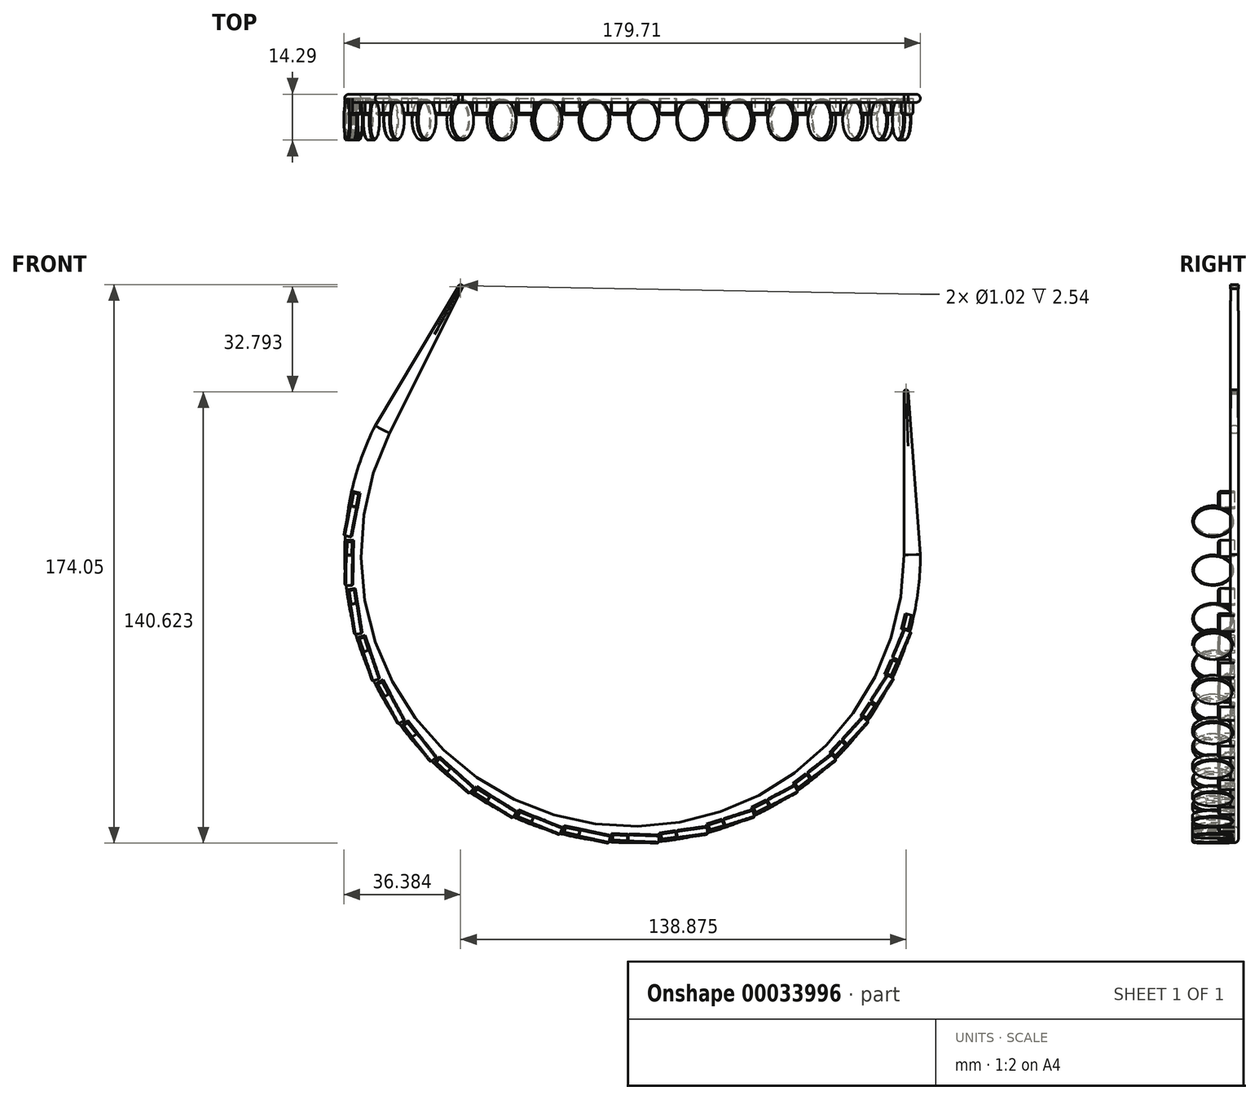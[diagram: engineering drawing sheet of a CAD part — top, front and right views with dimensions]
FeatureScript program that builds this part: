
annotation { "Feature Type Name" : "Feature", "Feature Type Description" : "" }
export const myFeature = defineFeature(function(context is Context, id is Id, definition is map)
    precondition{}
    {
        {
            var Q0;
            Q0=qCreatedBy(makeId("Front.planeOp"),FACE);
            var sketch = newSketch(context, id + "F0", { "sketchPlane" : qUnion([Q0])});
            skArc(sketch, "E0", {"start": v(-188.33, 16.19) * mm, "mid": v(-128.74, -111.39) * mm, "end": v(-18.36, -23.95) * mm});
            skArc(sketch, "E1", {"start": v(-23.44, -24.04) * mm, "mid": v(-127.57, -106.44) * mm, "end": v(-183.83, 13.83) * mm});
            skLineSegment(sketch, "E2", {"start": v(-183.83, 13.83) * mm, "end": v(-161.1, 59.27) * mm});
            skLineSegment(sketch, "E3", {"start": v(-188.33, 16.19) * mm, "end": v(-162.27, 59.79) * mm});
            skLineSegment(sketch, "E4", {"start": v(-162.27, 59.79) * mm, "end": v(-161.1, 59.27) * mm});
            skLineSegment(sketch, "E5", {"start": v(-18.36, -23.95) * mm, "end": v(-22.17, 26.7) * mm});
            skLineSegment(sketch, "E6", {"start": v(-23.44, -24.04) * mm, "end": v(-23.44, 26.76) * mm});
            skLineSegment(sketch, "E7", {"start": v(-23.44, 26.76) * mm, "end": v(-22.17, 26.7) * mm});
            skLineSegment(sketch, "E8", {"start": v(-188.33, 16.19) * mm, "end": v(-183.83, 13.83) * mm});
            skLineSegment(sketch, "E9", {"start": v(-23.44, -24.04) * mm, "end": v(-18.36, -23.95) * mm});
            skSolve(sketch);
        }
        {
            var Q0;
            Q0=makeQuery(id+"F0.imprint","IMPRINT",FACE,{"disambiguationData":[TD([[makeQuery(id+"F0.imprint","IMPRINT",EDGE,{"derivedFrom":sQuery(id+"F0.wireOp",EDGE,"E0")}),1.0]])]});
            var sketch = newSketch(context, id + "F1", { "sketchPlane" : qUnion([Q0])});
            skSolve(sketch);
        }
        {
            var Q0;
            Q0=makeQuery(id+"F1.imprint","IMPRINT",FACE,{"disambiguationData":[TD([[makeQuery(id+"F1.imprint","IMPRINT",EDGE,{"derivedFrom":makeQuery(id+"F0.imprint","IMPRINT",EDGE,{"derivedFrom":sQuery(id+"F0.wireOp",EDGE,"E0")})}),1.0]])]});
            extrude(context, id + "F2", {"entities" : qUnion([Q0]), "depth" : 2.54 * mm});
        }
        {
            var Q0;
            Q0=makeQuery(id+"F0.imprint","IMPRINT",FACE,{"disambiguationData":[TD([[makeQuery(id+"F0.imprint","IMPRINT",EDGE,{"derivedFrom":sQuery(id+"F0.wireOp",EDGE,"E2")}),1.0]])]});
            var sketch = newSketch(context, id + "F3", { "sketchPlane" : qUnion([Q0])});
            skCircle(sketch, "E10", {"center": v(-161.69, 59.53) * mm, "radius": 0.63 * mm});
            skPoint(sketch, "E10.first.point", {"position": v(-162.3, 59.7) * mm});
            skPoint(sketch, "E10.second.point", {"position": v(-161.15, 59.2) * mm});
            skPoint(sketch, "E10.third.point", {"position": v(-161.2, 59.93) * mm});
            skCircle(sketch, "E11", {"center": v(-161.69, 59.53) * mm, "radius": 0.5 * mm});
            skSolve(sketch);
        }
        {
            var Q0;
            Q0 = qSketchRegion(id + "F3", true);
            extrude(context, id + "F4", {"entities" : qUnion([Q0]), "depth" : 2.54 * mm});
        }
        {
            var Q0;
            Q0=makeQuery(id+"F0.imprint","IMPRINT",FACE,{"disambiguationData":[TD([[makeQuery(id+"F0.imprint","IMPRINT",EDGE,{"derivedFrom":sQuery(id+"F0.wireOp",EDGE,"E5")}),1.0]])]});
            var sketch = newSketch(context, id + "F5", { "sketchPlane" : qUnion([Q0])});
            skCircle(sketch, "E12", {"center": v(-22.81, 26.73) * mm, "radius": 0.63 * mm});
            skPoint(sketch, "E12.first.point", {"position": v(-23.44, 26.78) * mm});
            skPoint(sketch, "E12.second.point", {"position": v(-22.18, 26.72) * mm});
            skPoint(sketch, "E12.third.point", {"position": v(-22.6, 27.33) * mm});
            skCircle(sketch, "E13", {"center": v(-22.81, 26.73) * mm, "radius": 0.5 * mm});
            skSolve(sketch);
        }
        {
            var Q0;
            Q0 = qSketchRegion(id + "F5", true);
            extrude(context, id + "F6", {"entities" : qUnion([Q0]), "depth" : 2.54 * mm});
        }
        {
            var Q0;
            Q0=makeQuery(id+"F0.imprint","IMPRINT",FACE,{"disambiguationData":[TD([[makeQuery(id+"F0.imprint","IMPRINT",EDGE,{"derivedFrom":sQuery(id+"F0.wireOp",EDGE,"E5")}),1.0]])]});
            var Q1;
            Q1=makeQuery(id+"F0.imprint","IMPRINT",FACE,{"disambiguationData":[TD([[makeQuery(id+"F0.imprint","IMPRINT",EDGE,{"derivedFrom":sQuery(id+"F0.wireOp",EDGE,"E2")}),1.0]])]});
            extrude(context, id + "F7", {"entities" : qUnion([Q0, Q1]), "depth" : 2.54 * mm});
        }
        {
            var Q0;
            Q0=makeQuery(id+"F7.opExtrude","SWEPT_FACE",FACE,{"disambiguationData":[OSD([sQuery(id+"F0.wireOp",EDGE,"E3")])]});
            var sketch = newSketch(context, id + "F8", { "sketchPlane" : qUnion([Q0])});
            skEllipse(sketch, "E14", {"center": v(7.94, -82.75) * mm, "majorRadius": 6.35 * mm, "minorRadius": 4.76 * mm, "majorAxis": v(1, 0)});
            skSolve(sketch);
        }
        {
            var Q0;
            {var subQ0=sQuery(id+"F8.wireOp",EDGE,"E14");var subQ1=sQuery(id+"F0.wireOp",EDGE,"E3");var subQ4=makeQuery(id+"F7.opExtrude","CAP_EDGE",EDGE,{"disambiguationData":[OSD([subQ1])],"isStart":false});var subQ5=makeQuery(id+"F8.imprint","INTERSECT",VERTEX,{"derivedFrom":[subQ4,subQ0]});Q0=makeQuery(id+"F8.imprint","IMPRINT",FACE,{"disambiguationData":[TD([[makeQuery(id+"F8.imprint","IMPRINT",EDGE,{"disambiguationData":[TD([[subQ5,1.0]])],"derivedFrom":subQ0}),1.0]])]});}
            var Q1;
            {var subQ0=sQuery(id+"F8.wireOp",EDGE,"E14");var subQ1=sQuery(id+"F0.wireOp",EDGE,"E3");var subQ4=makeQuery(id+"F7.opExtrude","CAP_EDGE",EDGE,{"disambiguationData":[OSD([subQ1])],"isStart":false});var subQ5=makeQuery(id+"F8.imprint","INTERSECT",VERTEX,{"derivedFrom":[subQ4,subQ0]});Q1=makeQuery(id+"F8.imprint","IMPRINT",FACE,{"disambiguationData":[TD([[makeQuery(id+"F8.imprint","IMPRINT",EDGE,{"disambiguationData":[TD([[subQ5,-1.0]])],"derivedFrom":subQ0}),1.0]])]});}
            extrude(context, id + "F9", {"entities" : qUnion([Q0, Q1]), "oppositeDirection" : true, "depth" : 2.54 * mm});
        }
        {
            var Q0;
            Q0=makeQuery(id+"F9.opExtrude","CAP_EDGE",EDGE,{"disambiguationData":[OSD([sQuery(id+"F8.wireOp",EDGE,"E14")])],"isStart":true});
            var Q1;
            Q1=makeQuery(id+"F9.opExtrude","CAP_EDGE",EDGE,{"disambiguationData":[OSD([sQuery(id+"F8.wireOp",EDGE,"E14")])],"isStart":false});
            chamfer(context, id + "F10", {"entities" : qUnion([Q0, Q1]), "width" : 0.32 * mm, "tangentPropagation" : true});
        }
        {
            var Q0;
            Q0=makeQuery(id+"F2.opExtrude","CAP_EDGE",EDGE,{"disambiguationData":[OSD([sQuery(id+"F0.wireOp",EDGE,"E0")])],"isStart":true});
            var Q1;
            Q1=makeQuery(id+"F2.opExtrude","CAP_EDGE",EDGE,{"disambiguationData":[OSD([sQuery(id+"F0.wireOp",EDGE,"E0")])],"isStart":false});
            var Q2;
            Q2=makeQuery(id+"F2.opExtrude","CAP_EDGE",EDGE,{"disambiguationData":[OSD([sQuery(id+"F0.wireOp",EDGE,"E1")])],"isStart":false});
            var Q3;
            Q3=makeQuery(id+"F2.opExtrude","CAP_EDGE",EDGE,{"disambiguationData":[OSD([sQuery(id+"F0.wireOp",EDGE,"E1")])],"isStart":true});
            fillet(context, id + "F11", {"entities" : qUnion([Q0, Q1, Q2, Q3]), "radius" : 1.27 * mm, "tangentPropagation" : true, "allowEdgeOverflow" : false});
        }
        {
            var Q0;
            Q0=makeQuery(id+"F7.opExtrude","CAP_EDGE",EDGE,{"disambiguationData":[OSD([sQuery(id+"F0.wireOp",EDGE,"E6")])],"isStart":true});
            var Q1;
            Q1=makeQuery(id+"F7.opExtrude","CAP_EDGE",EDGE,{"disambiguationData":[OSD([sQuery(id+"F0.wireOp",EDGE,"E6")])],"isStart":false});
            var Q2;
            Q2=makeQuery(id+"F7.opExtrude","CAP_EDGE",EDGE,{"disambiguationData":[OSD([sQuery(id+"F0.wireOp",EDGE,"E5")])],"isStart":false});
            var Q3;
            Q3=makeQuery(id+"F7.opExtrude","CAP_EDGE",EDGE,{"disambiguationData":[OSD([sQuery(id+"F0.wireOp",EDGE,"E3")])],"isStart":true});
            var Q4;
            Q4=makeQuery(id+"F7.opExtrude","CAP_EDGE",EDGE,{"disambiguationData":[OSD([sQuery(id+"F0.wireOp",EDGE,"E3")])],"isStart":false});
            var Q5;
            Q5=makeQuery(id+"F7.opExtrude","CAP_EDGE",EDGE,{"disambiguationData":[OSD([sQuery(id+"F0.wireOp",EDGE,"E2")])],"isStart":false});
            var Q6;
            Q6=makeQuery(id+"F7.opExtrude","CAP_EDGE",EDGE,{"disambiguationData":[OSD([sQuery(id+"F0.wireOp",EDGE,"E2")])],"isStart":true});
            var Q7;
            Q7=makeQuery(id+"F7.opExtrude","CAP_EDGE",EDGE,{"disambiguationData":[OSD([sQuery(id+"F0.wireOp",EDGE,"E5")])],"isStart":true});
            fillet(context, id + "F12", {"entities" : qUnion([Q0, Q1, Q2, Q3, Q4, Q5, Q6, Q7]), "radius" : 1.27 * mm, "tangentPropagation" : true, "allowEdgeOverflow" : false});
        }
        {
            var Q0;
            Q0=makeQuery(id+"F9.opExtrude","SWEPT_BODY",BODY,{"disambiguationData":[OSD([sQuery(id+"F8.wireOp",EDGE,"E14")])]});
            var Q1;
            Q1=makeQuery(id+"F11.opFillet","BLEND_FACE",FACE,{"disambiguationData":[OSD([sQuery(id+"F0.wireOp",EDGE,"E0")])]});
            circularPattern(context, id + "F13", {"entities" : qUnion([Q0]), "axis" : qUnion([Q1]), "angle" : 9.9 * degree, "instanceCount" : 22});
        }
        {
            var Q0;
            Q0=makeQuery(id+"F13.opPattern","COPY",FACE,{"derivedFrom":makeQuery(id+"F9.opExtrude","CAP_FACE",FACE,{"disambiguationData":[OSD([sQuery(id+"F8.wireOp",EDGE,"E14")])],"isStart":true}),"instanceName":"2"});
            var sketch = newSketch(context, id + "F14", { "sketchPlane" : qUnion([Q0])});
            skLineSegment(sketch, "E15.bottom", {"start": v(1.27, -41.7) * mm, "end": v(6.35, -41.7) * mm});
            skLineSegment(sketch, "E15.top", {"start": v(1.27, -46.77) * mm, "end": v(6.35, -46.77) * mm});
            skLineSegment(sketch, "E15.left", {"start": v(1.27, -41.7) * mm, "end": v(1.27, -46.77) * mm});
            skLineSegment(sketch, "E15.right", {"start": v(6.35, -41.7) * mm, "end": v(6.35, -46.77) * mm});
            skSolve(sketch);
        }
        {
            var Q0;
            Q0 = qSketchRegion(id + "F14", true);
            extrude(context, id + "F15", {"entities" : qUnion([Q0]), "oppositeDirection" : true, "depth" : 2.54 * mm});
        }
        {
            var Q0;
            Q0=makeQuery(id+"F15.opExtrude","CAP_EDGE",EDGE,{"disambiguationData":[OSD([sQuery(id+"F14.wireOp",EDGE,"E15.right")])],"isStart":true});
            var Q1;
            Q1=makeQuery(id+"F15.opExtrude","CAP_EDGE",EDGE,{"disambiguationData":[OSD([sQuery(id+"F14.wireOp",EDGE,"E15.right")])],"isStart":false});
            var Q2;
            Q2=makeQuery(id+"F15.opExtrude","SWEPT_EDGE",EDGE,{"disambiguationData":[OSD([sQuery(id+"F14.wireOp",EDGE,"E15.bottom"),sQuery(id+"F14.wireOp",EDGE,"E15.right")])]});
            chamfer(context, id + "F16", {"entities" : qUnion([Q0, Q1, Q2]), "width" : 0.5 * mm, "tangentPropagation" : true});
        }
        {
            var Q0;
            Q0=makeQuery(id+"F15.opExtrude","SWEPT_BODY",BODY,{"disambiguationData":[OSD([sQuery(id+"F14.wireOp",EDGE,"E15.bottom"),sQuery(id+"F14.wireOp",EDGE,"E15.top"),sQuery(id+"F14.wireOp",EDGE,"E15.left"),sQuery(id+"F14.wireOp",EDGE,"E15.right")])]});
            var Q1;
            Q1=makeQuery(id+"F11.opFillet","BLEND_FACE",FACE,{"disambiguationData":[OSD([sQuery(id+"F0.wireOp",EDGE,"E0")])]});
            circularPattern(context, id + "F17", {"entities" : qUnion([Q0]), "axis" : qUnion([Q1]), "angle" : 9.85 * degree, "instanceCount" : 19});
        }
        {
            var Q0;
            Q0=makeQuery(id+"F13.opPattern","COPY",BODY,{"derivedFrom":makeQuery(id+"F9.opExtrude","SWEPT_BODY",BODY,{"disambiguationData":[OSD([sQuery(id+"F8.wireOp",EDGE,"E14")])]}),"instanceName":"21"});
            deleteBodies(context, id + "F18", {"entities" : qUnion([Q0])});
        }
        {
            var Q0;
            Q0=makeQuery(id+"F13.opPattern","COPY",BODY,{"derivedFrom":makeQuery(id+"F9.opExtrude","SWEPT_BODY",BODY,{"disambiguationData":[OSD([sQuery(id+"F8.wireOp",EDGE,"E14")])]}),"instanceName":"20"});
            deleteBodies(context, id + "F19", {"entities" : qUnion([Q0])});
        }
        {
            var Q0;
            Q0=makeQuery(id+"F13.opPattern","COPY",BODY,{"derivedFrom":makeQuery(id+"F9.opExtrude","SWEPT_BODY",BODY,{"disambiguationData":[OSD([sQuery(id+"F8.wireOp",EDGE,"E14")])]}),"instanceName":"1"});
            deleteBodies(context, id + "F20", {"entities" : qUnion([Q0])});
        }
        {
            var Q0;
            Q0=makeQuery(id+"F9.opExtrude","SWEPT_BODY",BODY,{"disambiguationData":[OSD([sQuery(id+"F8.wireOp",EDGE,"E14")])]});
            deleteBodies(context, id + "F21", {"entities" : qUnion([Q0])});
        }
    });
